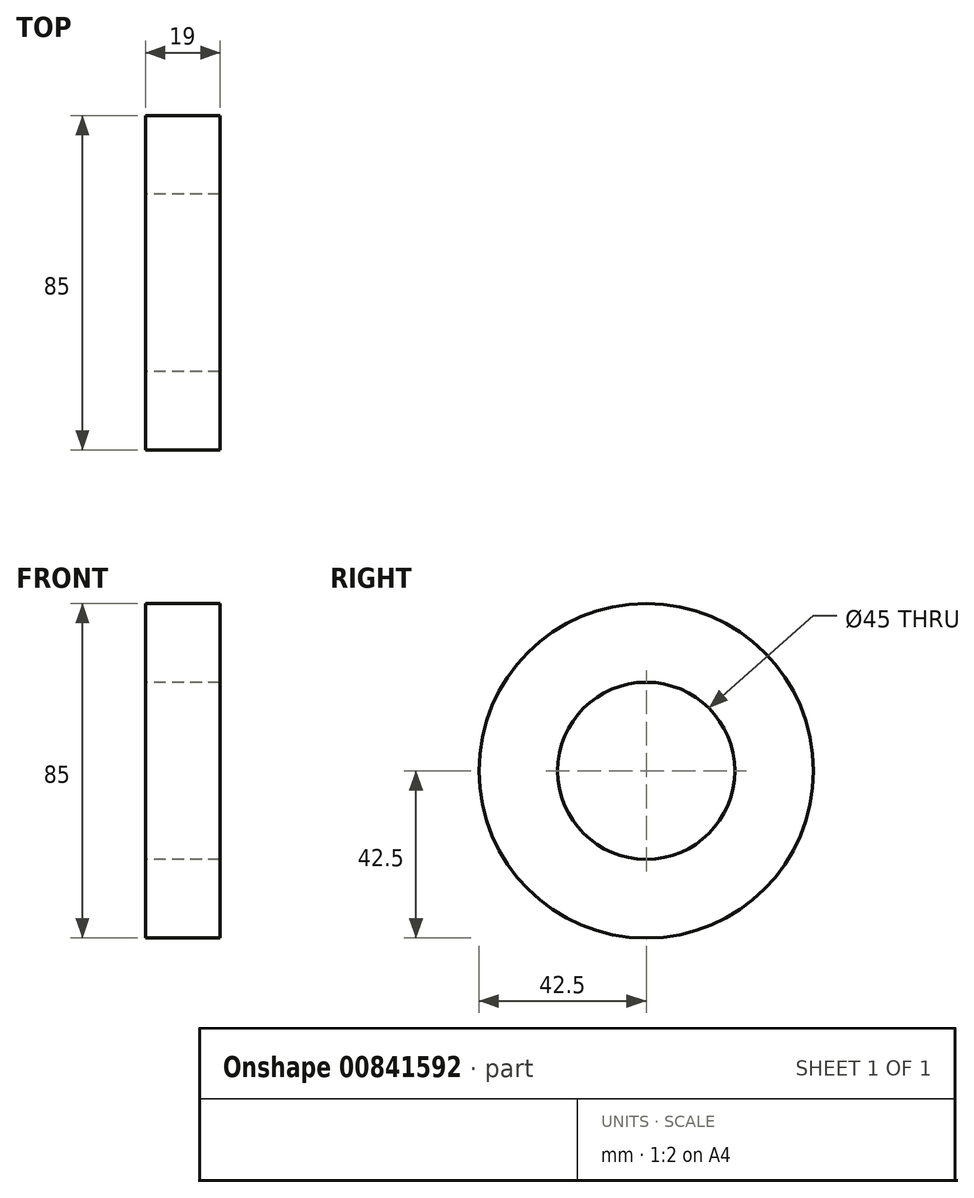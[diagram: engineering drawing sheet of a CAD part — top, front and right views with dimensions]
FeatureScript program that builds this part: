
annotation { "Feature Type Name" : "Feature", "Feature Type Description" : "" }
export const myFeature = defineFeature(function(context is Context, id is Id, definition is map)
    precondition{}
    {
        {
            var Q0;
            Q0=qCreatedBy(makeId("Front.planeOp"),FACE);
            var sketch = newSketch(context, id + "F0", { "sketchPlane" : qUnion([Q0])});
            skLineSegment(sketch, "E0", {"start": v(0, 42.5) * mm, "end": v(19, 42.5) * mm});
            skLineSegment(sketch, "E1", {"start": v(19, 42.5) * mm, "end": v(19, 22.5) * mm});
            skLineSegment(sketch, "E2", {"start": v(19, 22.5) * mm, "end": v(0, 22.5) * mm});
            skLineSegment(sketch, "E3", {"start": v(0, 22.5) * mm, "end": v(0, 42.5) * mm});
            skLineSegment(sketch, "E4", {"start": v(0, 0) * mm, "end": v(33.55, 0) * mm, "construction": true});
            skSolve(sketch);
        }
        {
            var Q0;
            Q0=makeQuery(id+"F0.imprint","IMPRINT",FACE,{"disambiguationData":[TD([[makeQuery(id+"F0.imprint","IMPRINT",EDGE,{"derivedFrom":sQuery(id+"F0.wireOp",EDGE,"E0")}),-1.0]])]});
            var Q1;
            Q1=sQuery(id+"F0.wireOp",EDGE,"E4");
            revolve(context, id + "F1", {"surfaceOperationType" : NewSurfaceOperationType.NEW, "entities" : qUnion([Q0]), "axis" : qUnion([Q1]), "revolveType" : RevolveType.FULL});
        }
    });
